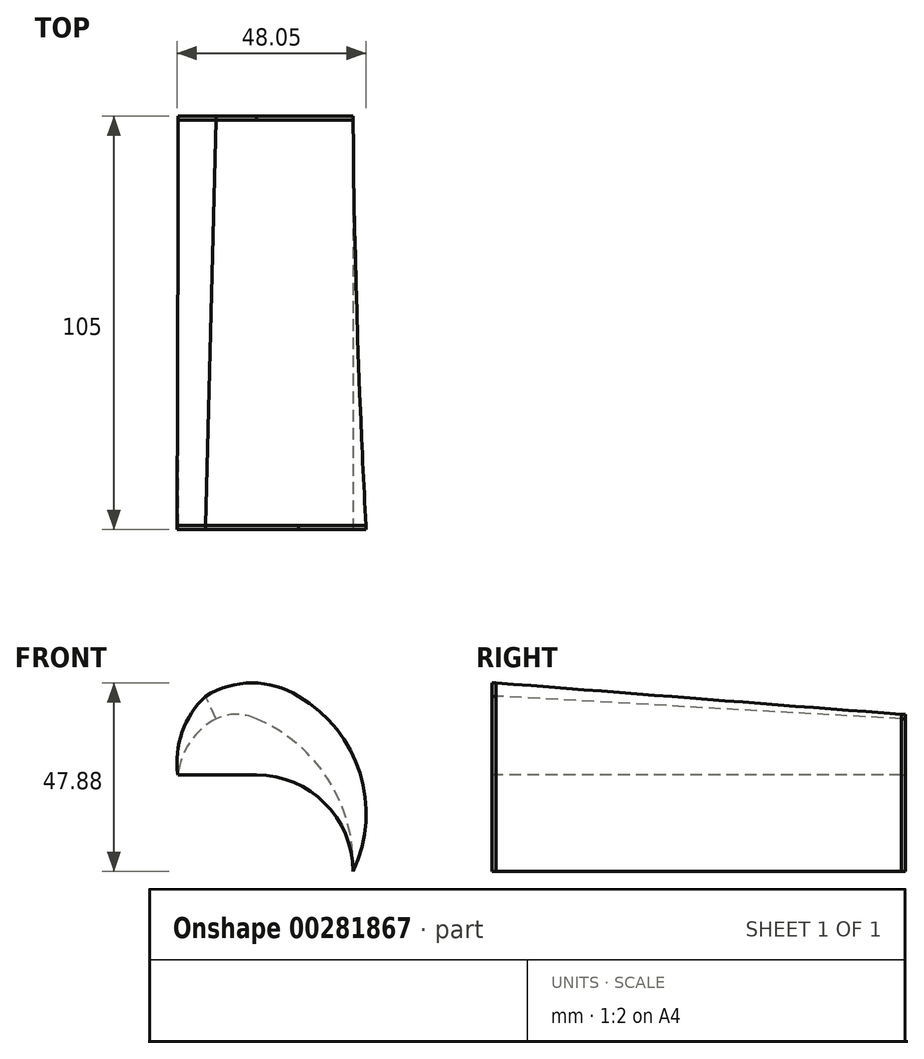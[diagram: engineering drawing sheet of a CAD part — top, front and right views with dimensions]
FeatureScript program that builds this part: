
annotation { "Feature Type Name" : "Feature", "Feature Type Description" : "" }
export const myFeature = defineFeature(function(context is Context, id is Id, definition is map)
    precondition{}
    {
        {
            var Q0;
            Q0=qCreatedBy(makeId("Front.planeOp"),FACE);
            var sketch = newSketch(context, id + "F0", { "sketchPlane" : qUnion([Q0])});
            skLineSegment(sketch, "E0.bottom", {"start": v(0, 0) * mm, "end": v(-59.26, 0) * mm, "construction": true});
            skLineSegment(sketch, "E0.top", {"start": v(0, 24.5) * mm, "end": v(-59.26, 24.5) * mm, "construction": true});
            skLineSegment(sketch, "E0.left", {"start": v(0, 0) * mm, "end": v(0, 24.5) * mm, "construction": true});
            skLineSegment(sketch, "E0.right", {"start": v(-59.26, 0) * mm, "end": v(-59.26, 24.5) * mm, "construction": true});
            skLineSegment(sketch, "E1", {"start": v(0, 0) * mm, "end": v(24.5, 0) * mm, "construction": true});
            skArc(sketch, "E2", {"start": v(24.5, 0) * mm, "mid": v(17.32, 17.32) * mm, "end": v(0, 24.5) * mm});
            skLineSegment(sketch, "E3", {"start": v(0, 24.5) * mm, "end": v(-20, 24.5) * mm});
            skLineSegment(sketch, "E4.bottom", {"start": v(0, 24.5) * mm, "end": v(-12.9, 24.5) * mm});
            skArc(sketch, "E5", {"start": v(-12.9, 44.5) * mm, "mid": v(-18.92, 35.38) * mm, "end": v(-20, 24.5) * mm});
            skArc(sketch, "E6", {"start": v(10.62, 44.5) * mm, "mid": v(-1.14, 47.88) * mm, "end": v(-12.9, 44.5) * mm});
            skArc(sketch, "E7", {"start": v(24.5, 0) * mm, "mid": v(26.26, 24.96) * mm, "end": v(10.62, 44.5) * mm});
            skSolve(sketch);
        }
        {
            var Q0;
            Q0=qCreatedBy(makeId("Front.planeOp"),FACE);
            cPlane(context, id + "F1", {"entities" : qUnion([Q0]), "cplaneType" : CPlaneType.OFFSET, "offset" : 105 * mm, "oppositeDirection" : true, "width" : 150 * mm, "height" : 150 * mm});
        }
        {
            var Q0;
            Q0=qCreatedBy(id+"F1.planeOp",FACE);
            var sketch = newSketch(context, id + "F2", { "sketchPlane" : qUnion([Q0])});
            skLineSegment(sketch, "E8", {"start": v(0, 24.5) * mm, "end": v(-20, 24.5) * mm});
            skArc(sketch, "E9", {"start": v(24.5, 0) * mm, "mid": v(17.32, 17.32) * mm, "end": v(0, 24.5) * mm});
            skLineSegment(sketch, "E10.bottom", {"start": v(0, 24.5) * mm, "end": v(-10.27, 24.5) * mm, "construction": true});
            skLineSegment(sketch, "E10.top", {"start": v(0, 38.78) * mm, "end": v(-10.27, 38.78) * mm, "construction": true});
            skLineSegment(sketch, "E10.left", {"start": v(0, 24.5) * mm, "end": v(0, 38.78) * mm, "construction": true});
            skLineSegment(sketch, "E10.right", {"start": v(-10.27, 24.5) * mm, "end": v(-10.27, 38.78) * mm, "construction": true});
            skArc(sketch, "E11", {"start": v(-10.27, 38.78) * mm, "mid": v(-16.9, 32.84) * mm, "end": v(-20, 24.5) * mm});
            skArc(sketch, "E12", {"start": v(0, 38.78) * mm, "mid": v(-5.14, 39.89) * mm, "end": v(-10.27, 38.78) * mm});
            skArc(sketch, "E13", {"start": v(24.5, 0) * mm, "mid": v(18.31, 23.22) * mm, "end": v(0, 38.78) * mm});
            skSolve(sketch);
        }
        {
            var Q0;
            Q0 = qSketchRegion(id + "F0", true);
            extrude(context, id + "F3", {"entities" : qUnion([Q0]), "oppositeDirection" : true, "depth" : 1 * mm});
        }
        {
            var Q0;
            Q0 = qSketchRegion(id + "F2", true);
            extrude(context, id + "F4", {"entities" : qUnion([Q0]), "depth" : 1 * mm});
        }
        {
            var Q0;
            Q0=makeQuery(id+"F4.opExtrude","CAP_FACE",FACE,{"disambiguationData":[OSD([sQuery(id+"F2.wireOp",EDGE,"E8"),sQuery(id+"F2.wireOp",EDGE,"E9"),sQuery(id+"F2.wireOp",EDGE,"E11"),sQuery(id+"F2.wireOp",EDGE,"E12"),sQuery(id+"F2.wireOp",EDGE,"E13")])],"isStart":false});
            var Q1;
            Q1=makeQuery(id+"F3.opExtrude","CAP_FACE",FACE,{"disambiguationData":[OSD([sQuery(id+"F0.wireOp",EDGE,"E2"),sQuery(id+"F0.wireOp",EDGE,"E3"),sQuery(id+"F0.wireOp",EDGE,"E4.bottom"),sQuery(id+"F0.wireOp",EDGE,"E5"),sQuery(id+"F0.wireOp",EDGE,"E6"),sQuery(id+"F0.wireOp",EDGE,"E7")])],"isStart":false});
            loft(context, id + "F5", {"sheetProfilesArray" : [{ "sheetProfileEntities" : qUnion([Q0]) }, { "sheetProfileEntities" : qUnion([Q1]) }]});
        }
    });
